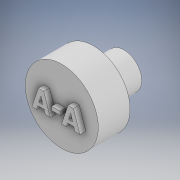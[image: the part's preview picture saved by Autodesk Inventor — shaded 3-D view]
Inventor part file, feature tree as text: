
AUTODESK INVENTOR PART (.ipt)
format: ipt  version: 2022 (Build 260153000, 153)  size: 151,552 bytes
history: native  units: in
note: dims shown in document units (in); Inventor stores cm internally (conversion verified against a paired STEP export)
features: sketch x3, extrude x3
ambient origin geometry x8: Origin, YZ Plane, XZ Plane, XY Plane, X Axis, Y Axis, Z Axis, Center Point
bodies: Solid1 (feature_tree)
feature tree (6):
  sketch  "Sketch1"  dims[d0=0.4898in d1=0.0185in]
  extrude  "Extrusion1"  Depth=0.0185in
  extrude  "Extrusion2"  Depth=0.189in TaperAngle=0.0deg
  sketch  "Sketch2"  dims[d2=0.1969in d3=0.0in d4=0.189in d5=0.0in]
  extrude  "Extrusion6"  [1 undecoded]
  sketch  "Sketch3"  dims[d12=0.0354in d13=0.0in]
note: 1 required parameter value undecoded (feature->parameter linkage not recoverable at this tier; creation-order binding heuristic only, values carry confidence <= 0.55)
